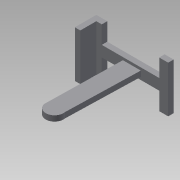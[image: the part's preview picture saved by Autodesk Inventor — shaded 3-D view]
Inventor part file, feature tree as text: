
AUTODESK INVENTOR PART (.ipt)
format: ipt  version: 2015 SP1 (Build 190203100, 203)  size: 133,632 bytes
history: native  units: mm
features: extrude x5, sketch x4, plane x2
ambient origin geometry x8: Origin, YZ Plane, XZ Plane, XY Plane, X Axis, Y Axis, Z Axis, Center Point
bodies: Solid1 (feature_tree)
feature tree (11):
  plane  "Work Plane5"
  sketch  "Sketch4"  dims[d34=15.0mm d36=2.0mm]
  extrude  "Extrusion7"  Depth=2.0mm
  extrude  "Extrusion8"  Depth=17.0mm TaperAngle=0.0deg
  plane  "Work Plane4"
  extrude  "Extrusion9"  Depth=2.0mm
  extrude  "Extrusion10"  Depth=2.0mm
  extrude  "Extrusion11"  Depth=2.0mm
  sketch  "Sketch5"  dims[d37=2.0mm d38=0.0mm d39=17.0mm d40=0.0mm]
  sketch  "Sketch6"  dims[d41=17.0mm d42=0.0mm d43=2.0mm]
  sketch  "Sketch7"  dims[d44=2.0mm d45=2.0mm d46=2.0mm d47=2.0mm d48=0.0mm d49=5.0mm d50=2.0mm d51=0.0mm]
